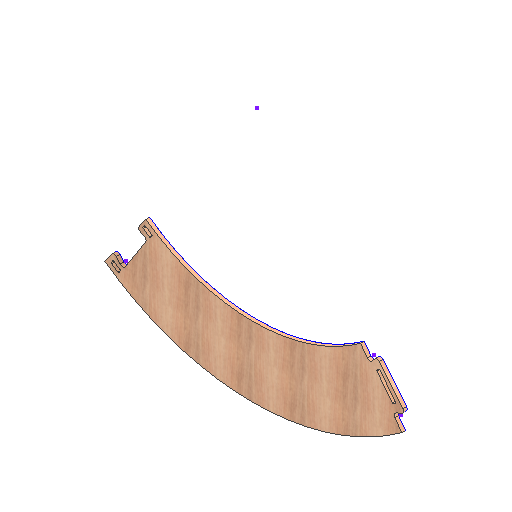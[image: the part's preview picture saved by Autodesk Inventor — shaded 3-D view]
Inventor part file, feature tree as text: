
AUTODESK INVENTOR PART (.ipt)
format: ipt  version: 2021 (Build 250183000, 183)  size: 261,632 bytes
history: native  units: mm
features: other x2, extrude x2, hole x1
ambient origin geometry x8: Origin, YZ Plane, XZ Plane, XY Plane, X Axis, Y Axis, Z Axis, Center Point
bodies: Solid1 (feature_tree)
feature tree (5):
  other  "CONTOURS"
  hole  "HOLES"  [1 undecoded]
  other  "LETTERS"
  extrude  "Extrusion2"  Depth=18.0mm TaperAngle=0.0deg
  extrude  "Extrusion3"  [1 undecoded]
note: 2 required parameter values undecoded (feature->parameter linkage not recoverable at this tier; creation-order binding heuristic only, values carry confidence <= 0.55)
